FCSTD DOCUMENT  (FreeCAD 1.0R38806 (Git))
Label: iis2iclx
License: All rights reserved
LicenseURL: http://en.wikipedia.org/wiki/All_rights_reserved
objects: Sketcher::SketchObject×3, PartDesign::Body×1
note: 7 computed .brp shape members not serialized (recipe doc carries the construction recipe); baked Part::Feature solids carry a one-line shape summary decoded from their .brp

FEATURE [Sketcher::SketchObject] Sketch  label="Pads_TH_SMD"
  ArcFitTolerance = 1e-06
  AttachmentSupport = -> [XY_Plane]
  FullyConstrained = true
  MakeInternals = false
  MapMode = 5
  sketch-geometry (101):
    g0: LineSegment [constr] StartX=-2.05 StartY=2.05 StartZ=0 EndX=-2.05 EndY=-2.05 EndZ=0
    g1: LineSegment [constr] StartX=-2.05 StartY=-2.05 StartZ=0 EndX=2.05 EndY=-2.05 EndZ=0
    g2: LineSegment [constr] StartX=2.05 StartY=-2.05 StartZ=0 EndX=2.05 EndY=2.05 EndZ=0
    g3: LineSegment [constr] StartX=2.05 StartY=2.05 StartZ=0 EndX=-2.05 EndY=2.05 EndZ=0
    g4: LineSegment StartX=1 StartY=-0.25 StartZ=0 EndX=1 EndY=-0.75 EndZ=0
    g5: LineSegment StartX=1 StartY=-0.75 StartZ=0 EndX=2.4 EndY=-0.75 EndZ=0
    g6: LineSegment StartX=2.4 StartY=-0.75 StartZ=0 EndX=2.4 EndY=-0.25 EndZ=0
    g7: LineSegment StartX=2.4 StartY=-0.25 StartZ=0 EndX=1 EndY=-0.25 EndZ=0
    g8: LineSegment StartX=1.7 StartY=0.75 StartZ=0 EndX=1.7 EndY=0.25 EndZ=0
    g9: LineSegment StartX=1.7 StartY=0.25 StartZ=0 EndX=2.4 EndY=0.25 EndZ=0
    g10: LineSegment StartX=2.4 StartY=0.25 StartZ=0 EndX=2.4 EndY=0.75 EndZ=0
    g11: LineSegment StartX=2.4 StartY=0.75 StartZ=0 EndX=1.7 EndY=0.75 EndZ=0
    g12: LineSegment [constr] StartX=2.4 StartY=2.4 StartZ=0 EndX=2.4 EndY=-2.4 EndZ=0
    g13: GeomPoint [constr] X=2.4 Y=0.5 Z=0
    g14: GeomPoint [constr] X=2.4 Y=-0.5 Z=0
    g15: LineSegment [constr] StartX=-2.05 StartY=1.92979 StartZ=0 EndX=1.92979 EndY=-2.05 EndZ=0
    g16: LineSegment [constr] StartX=-1.92979 StartY=2.05 StartZ=0 EndX=2.05 EndY=-1.92979 EndZ=0
    g17: LineSegment [constr] StartX=1.92979 StartY=2.05 StartZ=0 EndX=-2.05 EndY=-1.92979 EndZ=0
    g18: LineSegment [constr] StartX=-1.92979 StartY=-2.05 StartZ=0 EndX=2.05 EndY=1.92979 EndZ=0
    g19: LineSegment StartX=2.4 StartY=1.75 StartZ=0 EndX=1.87021 EndY=1.75 EndZ=0
    g20: LineSegment StartX=1.7 StartY=1.57979 StartZ=0 EndX=1.7 EndY=1.25 EndZ=0
    g21: LineSegment StartX=1.7 StartY=1.25 StartZ=0 EndX=2.4 EndY=1.25 EndZ=0
    g22: LineSegment StartX=2.4 StartY=1.25 StartZ=0 EndX=2.4 EndY=1.75 EndZ=0
    g23: GeomPoint [constr] X=2.4 Y=1.5 Z=0
    g24: LineSegment StartX=2.4 StartY=-1.25 StartZ=0 EndX=1.7 EndY=-1.25 EndZ=0
    g25: LineSegment StartX=1.7 StartY=-1.25 StartZ=0 EndX=1.7 EndY=-1.57979 EndZ=0
    g26: LineSegment StartX=1.87021 StartY=-1.75 StartZ=0 EndX=2.4 EndY=-1.75 EndZ=0
    g27: LineSegment StartX=2.4 StartY=-1.75 StartZ=0 EndX=2.4 EndY=-1.25 EndZ=0
    g28: GeomPoint [constr] X=2.4 Y=-1.5 Z=0
    g29: LineSegment StartX=1.7 StartY=1.57979 StartZ=0 EndX=1.87021 EndY=1.75 EndZ=0
    g30: LineSegment StartX=1.7 StartY=-1.57979 StartZ=0 EndX=1.87021 EndY=-1.75 EndZ=0
    g31: LineSegment [constr] StartX=2.4 StartY=2.4 StartZ=0 EndX=-2.4 EndY=2.4 EndZ=0
    g32: LineSegment [constr] StartX=-2.4 StartY=2.4 StartZ=0 EndX=-2.4 EndY=-2.4 EndZ=0
    g33: LineSegment [constr] StartX=-2.4 StartY=-2.4 StartZ=0 EndX=2.4 EndY=-2.4 EndZ=0
    g34: LineSegment StartX=1.75 StartY=2.4 StartZ=0 EndX=1.25 EndY=2.4 EndZ=0
    g35: LineSegment StartX=1.25 StartY=2.4 StartZ=0 EndX=1.25 EndY=1.7 EndZ=0
    g36: LineSegment StartX=1.25 StartY=1.7 StartZ=0 EndX=1.57979 EndY=1.7 EndZ=0
    g37: LineSegment StartX=1.75 StartY=1.87021 StartZ=0 EndX=1.75 EndY=2.4 EndZ=0
    g38: LineSegment StartX=0.75 StartY=2.4 StartZ=0 EndX=0.25 EndY=2.4 EndZ=0
    g39: LineSegment StartX=0.25 StartY=2.4 StartZ=0 EndX=0.25 EndY=1.7 EndZ=0
    g40: LineSegment StartX=0.25 StartY=1.7 StartZ=0 EndX=0.75 EndY=1.7 EndZ=0
    g41: LineSegment StartX=0.75 StartY=1.7 StartZ=0 EndX=0.75 EndY=2.4 EndZ=0
    g42: LineSegment StartX=-0.25 StartY=2.4 StartZ=0 EndX=-0.75 EndY=2.4 EndZ=0
    g43: LineSegment StartX=-0.75 StartY=2.4 StartZ=0 EndX=-0.75 EndY=1.7 EndZ=0
    g44: LineSegment StartX=-0.75 StartY=1.7 StartZ=0 EndX=-0.25 EndY=1.7 EndZ=0
    g45: LineSegment StartX=-0.25 StartY=1.7 StartZ=0 EndX=-0.25 EndY=2.4 EndZ=0
    g46: LineSegment StartX=-1.25 StartY=2.4 StartZ=0 EndX=-1.75 EndY=2.4 EndZ=0
    g47: LineSegment StartX=-1.75 StartY=2.4 StartZ=0 EndX=-1.75 EndY=1.87021 EndZ=0
    g48: LineSegment StartX=-1.57979 StartY=1.7 StartZ=0 EndX=-1.25 EndY=1.7 EndZ=0
    g49: LineSegment StartX=-1.25 StartY=1.7 StartZ=0 EndX=-1.25 EndY=2.4 EndZ=0
    g50: GeomPoint X=-1.5 Y=2.4 Z=0
    g51: GeomPoint X=-0.5 Y=2.4 Z=0
    g52: GeomPoint X=0.5 Y=2.4 Z=0
    g53: GeomPoint X=1.5 Y=2.4 Z=0
    g54: GeomPoint X=0.75 Y=2.05 Z=0
    g55: LineSegment StartX=-1.75 StartY=1.87021 StartZ=0 EndX=-1.57979 EndY=1.7 EndZ=0
    g56: LineSegment StartX=1.57979 StartY=1.7 StartZ=0 EndX=1.75 EndY=1.87021 EndZ=0
    g57: LineSegment StartX=-2.4 StartY=1.75 StartZ=0 EndX=-2.4 EndY=1.25 EndZ=0
    g58: LineSegment StartX=-2.4 StartY=1.25 StartZ=0 EndX=-1.7 EndY=1.25 EndZ=0
    g59: LineSegment StartX=-1.7 StartY=1.25 StartZ=0 EndX=-1.7 EndY=1.57979 EndZ=0
    g60: LineSegment StartX=-1.87021 StartY=1.75 StartZ=0 EndX=-2.4 EndY=1.75 EndZ=0
    g61: LineSegment StartX=-2.4 StartY=0.75 StartZ=0 EndX=-2.4 EndY=0.25 EndZ=0
    g62: LineSegment StartX=-2.4 StartY=0.25 StartZ=0 EndX=-1.7 EndY=0.25 EndZ=0
    g63: LineSegment StartX=-1.7 StartY=0.25 StartZ=0 EndX=-1.7 EndY=0.75 EndZ=0
    g64: LineSegment StartX=-1.7 StartY=0.75 StartZ=0 EndX=-2.4 EndY=0.75 EndZ=0
    g65: LineSegment StartX=-2.4 StartY=-0.25 StartZ=0 EndX=-2.4 EndY=-0.75 EndZ=0
    g66: LineSegment StartX=-2.4 StartY=-0.75 StartZ=0 EndX=-1.7 EndY=-0.75 EndZ=0
    g67: LineSegment StartX=-1.7 StartY=-0.75 StartZ=0 EndX=-1.7 EndY=-0.25 EndZ=0
    g68: LineSegment StartX=-1.7 StartY=-0.25 StartZ=0 EndX=-2.4 EndY=-0.25 EndZ=0
    g69: LineSegment StartX=-2.4 StartY=-1.25 StartZ=0 EndX=-2.4 EndY=-1.75 EndZ=0
    g70: LineSegment StartX=-2.4 StartY=-1.75 StartZ=0 EndX=-1.87021 EndY=-1.75 EndZ=0
    g71: LineSegment StartX=-1.7 StartY=-1.57979 StartZ=0 EndX=-1.7 EndY=-1.25 EndZ=0
    g72: LineSegment StartX=-1.7 StartY=-1.25 StartZ=0 EndX=-2.4 EndY=-1.25 EndZ=0
    g73: GeomPoint [constr] X=-2.4 Y=-1.5 Z=0
    g74: GeomPoint [constr] X=-2.4 Y=-0.5 Z=0
    g75: GeomPoint [constr] X=-2.4 Y=0.5 Z=0
    g76: GeomPoint [constr] X=-2.4 Y=1.5 Z=0
    g77: LineSegment StartX=-1.87021 StartY=1.75 StartZ=0 EndX=-1.7 EndY=1.57979 EndZ=0
    g78: LineSegment StartX=-1.87021 StartY=-1.75 StartZ=0 EndX=-1.7 EndY=-1.57979 EndZ=0
    g79: LineSegment StartX=-1.75 StartY=-2.4 StartZ=0 EndX=-1.25 EndY=-2.4 EndZ=0
    g80: LineSegment StartX=-1.25 StartY=-2.4 StartZ=0 EndX=-1.25 EndY=-1.7 EndZ=0
    g81: LineSegment StartX=-1.25 StartY=-1.7 StartZ=0 EndX=-1.57979 EndY=-1.7 EndZ=0
    g82: LineSegment StartX=-1.75 StartY=-1.87021 StartZ=0 EndX=-1.75 EndY=-2.4 EndZ=0
    g83: LineSegment StartX=-0.75 StartY=-2.4 StartZ=0 EndX=-0.25 EndY=-2.4 EndZ=0
    g84: LineSegment StartX=-0.25 StartY=-2.4 StartZ=0 EndX=-0.25 EndY=-1.7 EndZ=0
    g85: LineSegment StartX=-0.25 StartY=-1.7 StartZ=0 EndX=-0.75 EndY=-1.7 EndZ=0
    g86: LineSegment StartX=-0.75 StartY=-1.7 StartZ=0 EndX=-0.75 EndY=-2.4 EndZ=0
    g87: LineSegment StartX=0.25 StartY=-2.4 StartZ=0 EndX=0.75 EndY=-2.4 EndZ=0
    g88: LineSegment StartX=0.75 StartY=-2.4 StartZ=0 EndX=0.75 EndY=-1.7 EndZ=0
    g89: LineSegment StartX=0.75 StartY=-1.7 StartZ=0 EndX=0.25 EndY=-1.7 EndZ=0
    g90: LineSegment StartX=0.25 StartY=-1.7 StartZ=0 EndX=0.25 EndY=-2.4 EndZ=0
    g91: LineSegment StartX=1.25 StartY=-2.4 StartZ=0 EndX=1.75 EndY=-2.4 EndZ=0
    g92: LineSegment StartX=1.75 StartY=-2.4 StartZ=0 EndX=1.75 EndY=-1.87021 EndZ=0
    g93: LineSegment StartX=1.57979 StartY=-1.7 StartZ=0 EndX=1.25 EndY=-1.7 EndZ=0
    g94: LineSegment StartX=1.25 StartY=-1.7 StartZ=0 EndX=1.25 EndY=-2.4 EndZ=0
    g95: GeomPoint [constr] X=-1.5 Y=-2.4 Z=0
    g96: GeomPoint [constr] X=-0.5 Y=-2.4 Z=0
    g97: GeomPoint [constr] X=0.5 Y=-2.4 Z=0
    g98: GeomPoint [constr] X=1.5 Y=-2.4 Z=0
    g99: LineSegment StartX=-1.75 StartY=-1.87021 StartZ=0 EndX=-1.57979 EndY=-1.7 EndZ=0
    g100: LineSegment StartX=1.57979 StartY=-1.7 StartZ=0 EndX=1.75 EndY=-1.87021 EndZ=0
  constraints (282):
    c: Coincident(g0,g1)
    c: Coincident(g1,g2)
    c: Coincident(g2,g3)
    c: Coincident(g3,g0)
    c: Vertical(g0)
    c: Horizontal(g1)
    c: Symmetric(g2,g0,g-2)
    c: Symmetric(g2,g1,g-1)
    c: Equal(g3,g0)
    c: DistanceX(g3,g3) = 4.1
    c: Coincident(g4,g5)
    c: Coincident(g5,g6)
    c: Coincident(g6,g7)
    c: Coincident(g7,g4)
    c: Vertical(g4)
    c: Vertical(g6)
    c: Horizontal(g5)
    c: Horizontal(g7)
    c: Distance(g4,g6) = 1.4
    c: Distance(g5,g7) = 0.5
    c: Coincident(g8,g9)
    c: Coincident(g9,g10)
    c: Coincident(g10,g11)
    c: Coincident(g11,g8)
    c: Vertical(g8)
    c: Vertical(g10)
    c: Horizontal(g9)
    c: Distance(g8,g10) = 0.7
    c: Distance(g9,g11) = 0.5
    c: Symmetric(g10,g8,g2)
    c: Vertical(g12)
    c: PointOnObject(g10,g12)
    c: PointOnObject(g6,g12)
    c: Symmetric(g6,g6,g14)
    c: Symmetric(g10,g10,g13)
    c: DistanceY(g14,g13) = 1
    c: PointOnObject(g16,g2)
    c: PointOnObject(g15,g1)
    c: PointOnObject(g15,g0)
    c: PointOnObject(g16,g3)
    c: Parallel(g16,g15)
    c: Equal(g16,g15)
    c: Angle(g16,g3) = 0.785398
    c: Distance(g15,g16) = 0.17
    c: PointOnObject(g17,g3)
    c: PointOnObject(g17,g0)
    c: PointOnObject(g18,g1)
    c: PointOnObject(g18,g2)
    c: Parallel(g17,g18)
    c: Equal(g17,g18)
    c: Perpendicular(g16,g18)
    c: Distance(g17,g18) = 0.17
    c: Coincident(g20,g21)
    c: Coincident(g21,g22)
    c: Coincident(g22,g19)
    c: Horizontal(g19)
    c: Horizontal(g21)
    c: Vertical(g20)
    c: Vertical(g22)
    c: PointOnObject(g19,g12)
    c: Symmetric(g22,g22,g23)
    c: DistanceY(g13,g23) = 1
    c: Coincident(g24,g25)
    c: Coincident(g26,g27)
    c: Coincident(g27,g24)
    c: Horizontal(g24)
    c: Horizontal(g26)
    c: Vertical(g25)
    c: Vertical(g27)
    c: PointOnObject(g24,g12)
    c: Symmetric(g27,g27,g28)
    c: DistanceY(g28,g14) = 1
    c: Equal(g11,g21)
    c: Equal(g21,g24)
    c: Equal(g22,g10)
    c: Equal(g10,g27)
    c: DistanceY(g14,g-1) = 0.5
    c: PointOnObject(g29,g18)
    c: PointOnObject(g29,g18)
    c: PointOnObject(g29,g19)
    c: PointOnObject(g19,g18)
    c: Coincident(g20,g29)
    c: PointOnObject(g30,g16)
    c: PointOnObject(g30,g16)
    c: PointOnObject(g30,g26)
    c: PointOnObject(g30,g25)
    c: PointOnObject(g25,g16)
    c: PointOnObject(g26,g16)
    c: Coincident(g31,g12)
    c: Horizontal(g31)
    c: Coincident(g32,g31)
    c: Coincident(g33,g12)
    c: Horizontal(g33)
    c: Equal(g12,g33)
    c: Equal(g33,g32)
    c: Equal(g32,g31)
    c: Coincident(g34,g35)
    c: Coincident(g35,g36)
    c: Coincident(g37,g34)
    c: Horizontal(g34)
    c: Horizontal(g36)
    c: Vertical(g35)
    c: Vertical(g37)
    c: PointOnObject(g34,g31)
    c: Coincident(g38,g39)
    c: Coincident(g39,g40)
    c: Coincident(g40,g41)
    c: Coincident(g41,g38)
    c: Horizontal(g38)
    c: Horizontal(g40)
    c: Vertical(g39)
    c: Vertical(g41)
    c: PointOnObject(g38,g31)
    c: Coincident(g42,g43)
    c: Coincident(g43,g44)
    c: Coincident(g44,g45)
    c: Coincident(g45,g42)
    c: Horizontal(g42)
    c: Horizontal(g44)
    c: Vertical(g43)
    c: Vertical(g45)
    c: PointOnObject(g42,g31)
    c: Coincident(g46,g47)
    c: Coincident(g48,g49)
    c: Coincident(g49,g46)
    c: Horizontal(g46)
    c: Horizontal(g48)
    c: Vertical(g47)
    c: Vertical(g49)
    c: PointOnObject(g46,g31)
    c: Equal(g46,g42)
    c: Equal(g42,g38)
    c: Equal(g38,g34)
    c: Equal(g34,g22)
    c: Equal(g49,g45)
    c: Equal(g45,g39)
    c: Equal(g39,g35)
    c: Equal(g35,g11)
    c: Symmetric(g32,g31,g-1)
    c: Symmetric(g46,g46,g50)
    c: Symmetric(g42,g42,g51)
    c: Symmetric(g38,g38,g52)
    c: Symmetric(g34,g34,g53)
    c: Symmetric(g41,g41,g54)
    c: PointOnObject(g54,g3)
    c: DistanceX(g50,g51) = 1
    c: DistanceX(g51,g52) = 1
    c: DistanceX(g52,g53) = 1
    c: DistanceX(g-1,g52) = 0.5
    c: PointOnObject(g55,g16)
    c: PointOnObject(g55,g16)
    c: PointOnObject(g56,g17)
    c: PointOnObject(g56,g17)
    c: PointOnObject(g56,g36)
    c: PointOnObject(g56,g37)
    c: PointOnObject(g55,g47)
    c: PointOnObject(g55,g48)
    c: PointOnObject(g47,g16)
    c: PointOnObject(g48,g16)
    c: PointOnObject(g36,g17)
    c: PointOnObject(g37,g17)
    c: Coincident(g57,g58)
    c: Coincident(g58,g59)
    c: Coincident(g60,g57)
    c: Vertical(g57)
    c: Vertical(g59)
    c: Horizontal(g58)
    c: Horizontal(g60)
    c: PointOnObject(g57,g32)
    c: Coincident(g61,g62)
    c: Coincident(g62,g63)
    c: Coincident(g63,g64)
    c: Coincident(g64,g61)
    c: Vertical(g61)
    c: Vertical(g63)
    c: Horizontal(g62)
    c: Horizontal(g64)
    c: PointOnObject(g61,g32)
    c: Coincident(g65,g66)
    c: Coincident(g66,g67)
    c: Coincident(g67,g68)
    c: Coincident(g68,g65)
    c: Vertical(g65)
    c: Vertical(g67)
    c: Horizontal(g66)
    c: Horizontal(g68)
    c: PointOnObject(g65,g32)
    c: Coincident(g69,g70)
    c: Coincident(g71,g72)
    c: Coincident(g72,g69)
    c: Vertical(g69)
    c: Vertical(g71)
    c: Horizontal(g70)
    c: Horizontal(g72)
    c: PointOnObject(g69,g32)
    c: Equal(g69,g65)
    c: Equal(g65,g61)
    c: Equal(g61,g57)
    c: Equal(g57,g46)
    c: Equal(g72,g68)
    c: Equal(g68,g64)
    c: Equal(g64,g58)
    c: Equal(g58,g11)
    c: Symmetric(g69,g69,g73)
    c: Symmetric(g65,g65,g74)
    c: Symmetric(g61,g61,g75)
    c: Symmetric(g57,g57,g76)
    c: DistanceY(g73,g74) = 1
    c: DistanceY(g74,g75) = 1
    c: DistanceY(g75,g76) = 1
    c: DistanceY(g74,g-1) = 0.5
    c: PointOnObject(g77,g15)
    c: PointOnObject(g77,g15)
    c: PointOnObject(g78,g17)
    c: PointOnObject(g78,g17)
    c: PointOnObject(g78,g70)
    c: PointOnObject(g77,g59)
    c: Coincident(g60,g77)
    c: PointOnObject(g59,g15)
    c: PointOnObject(g70,g17)
    c: Coincident(g71,g78)
    c: Coincident(g79,g80)
    c: Coincident(g80,g81)
    c: Coincident(g82,g79)
    c: Horizontal(g79)
    c: Horizontal(g81)
    c: Vertical(g80)
    c: Vertical(g82)
    c: PointOnObject(g79,g33)
    c: Coincident(g83,g84)
    c: Coincident(g84,g85)
    c: Coincident(g85,g86)
    c: Coincident(g86,g83)
    c: Horizontal(g83)
    c: Horizontal(g85)
    c: Vertical(g84)
    c: Vertical(g86)
    c: PointOnObject(g83,g33)
    c: Coincident(g87,g88)
    c: Coincident(g88,g89)
    c: Coincident(g89,g90)
    c: Coincident(g90,g87)
    c: Horizontal(g87)
    c: Horizontal(g89)
    c: Vertical(g88)
    c: Vertical(g90)
    c: PointOnObject(g87,g33)
    c: Coincident(g91,g92)
    c: Coincident(g93,g94)
    c: Coincident(g94,g91)
    c: Horizontal(g91)
    c: Horizontal(g93)
    c: Vertical(g92)
    c: Vertical(g94)
    c: PointOnObject(g91,g33)
    c: Equal(g80,g84)
    c: Equal(g84,g90)
    c: Equal(g90,g94)
    c: Equal(g94,g9)
    c: Equal(g91,g87)
    c: Equal(g87,g83)
    c: Equal(g83,g79)
    c: Equal(g79,g10)
    c: Symmetric(g83,g83,g96)
    c: Symmetric(g87,g87,g97)
    c: Symmetric(g91,g91,g98)
    c: DistanceX(g97,g98) = 1
    c: DistanceX(g96,g97) = 1
    c: DistanceX(g-1,g97) = 0.5
    c: Symmetric(g79,g79,g95)
    c: DistanceX(g95,g96) = 1
    c: PointOnObject(g99,g18)
    c: PointOnObject(g99,g18)
    c: PointOnObject(g100,g15)
    c: PointOnObject(g100,g15)
    c: PointOnObject(g100,g92)
    c: PointOnObject(g99,g81)
    c: PointOnObject(g99,g82)
    c: PointOnObject(g82,g18)
    c: PointOnObject(g81,g18)
    c: Coincident(g93,g100)
    c: PointOnObject(g92,g15)
FEATURE [Sketcher::SketchObject] Sketch001  label="F_CtYrd_0.15"
  ArcFitTolerance = 1e-06
  AttachmentSupport = -> [XY_Plane]
  ExternalGeometry = -> [Sketch]
  FullyConstrained = true
  MakeInternals = false
  MapMode = 5
  sketch-geometry (4):
    g0: LineSegment StartX=-2.9 StartY=2.9 StartZ=0 EndX=-2.9 EndY=-2.9 EndZ=0
    g1: LineSegment StartX=-2.9 StartY=-2.9 StartZ=0 EndX=2.9 EndY=-2.9 EndZ=0
    g2: LineSegment StartX=2.9 StartY=-2.9 StartZ=0 EndX=2.9 EndY=2.9 EndZ=0
    g3: LineSegment StartX=2.9 StartY=2.9 StartZ=0 EndX=-2.9 EndY=2.9 EndZ=0
  constraints (12):
    c: Coincident(g0,g1)
    c: Coincident(g1,g2)
    c: Coincident(g2,g3)
    c: Coincident(g3,g0)
    c: Vertical(g0)
    c: Vertical(g2)
    c: Horizontal(g1)
    c: Horizontal(g3)
    c: DistanceX(g-6,g2) = 0.5
    c: DistanceY(g1,g-5) = 0.5
    c: DistanceX(g0,g-4) = 0.5
    c: DistanceY(g-3,g0) = 0.5
FEATURE [Sketcher::SketchObject] Sketch002  label="F_Silks_0.15"
  ArcFitTolerance = 1e-06
  AttachmentSupport = -> [XY_Plane]
  ExternalGeometry = -> [Sketch001]
  FullyConstrained = false
  MakeInternals = false
  MapMode = 5
  sketch-geometry (1):
    g0: Circle CenterX=2.9 CenterY=-0.484889 CenterZ=0 NormalX=0 NormalY=0 NormalZ=1 AngleXU=0 Radius=0.175
  constraints (2):
    c: PointOnObject(g0,g-3)
    c: Diameter(g0) = 0.35
FEATURE [PartDesign::Body] Body
  AllowCompound = false
  Group = -> [Sketch,Sketch001,Sketch002]
  Origin = -> Origin
